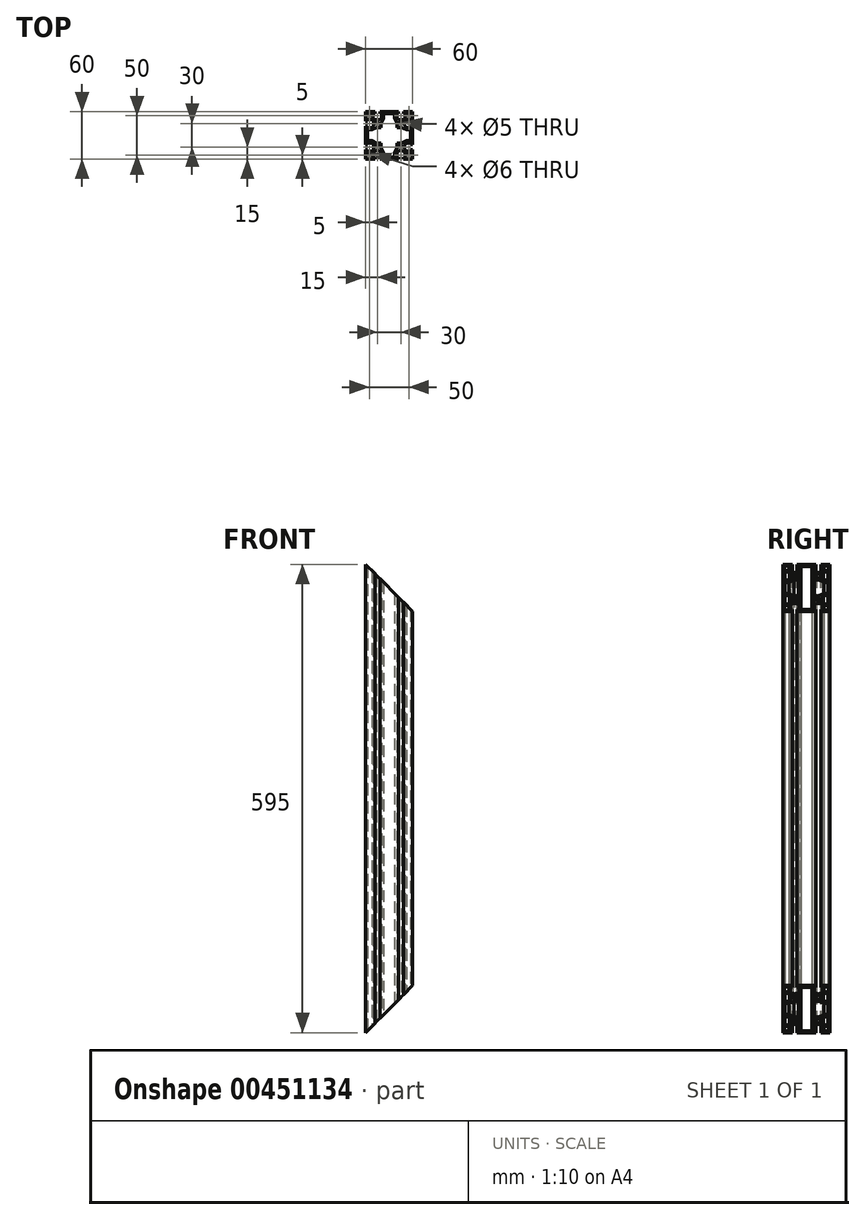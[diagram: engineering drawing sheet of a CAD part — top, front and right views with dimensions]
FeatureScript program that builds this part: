
annotation { "Feature Type Name" : "Feature", "Feature Type Description" : "" }
export const myFeature = defineFeature(function(context is Context, id is Id, definition is map)
    precondition{}
    {
        {
            var Q0;
            Q0=qCreatedBy(makeId("Top.planeOp"),FACE);
            var sketch = newSketch(context, id + "F0", { "sketchPlane" : qUnion([Q0])});
            skLineSegment(sketch, "E0.bottom", {"start": v(30, -30) * mm, "end": v(-30, -30) * mm});
            skLineSegment(sketch, "E0.top", {"start": v(30, 30) * mm, "end": v(-30, 30) * mm});
            skLineSegment(sketch, "E0.left", {"start": v(30, -30) * mm, "end": v(30, 30) * mm});
            skLineSegment(sketch, "E0.right", {"start": v(-30, -30) * mm, "end": v(-30, 30) * mm});
            skPoint(sketch, "E0.middle", {"position": v(0, 0) * mm});
            skLineSegment(sketch, "E1.top", {"start": v(-11.85, 30) * mm, "end": v(-18.15, 30) * mm});
            skLineSegment(sketch, "E1.left", {"start": v(-11.85, 27.5) * mm, "end": v(-11.85, 30) * mm});
            skLineSegment(sketch, "E1.right", {"start": v(-18.15, 27.5) * mm, "end": v(-18.15, 30) * mm});
            skPoint(sketch, "E1.middle", {"position": v(-15, 28.75) * mm});
            skLineSegment(sketch, "E2.bottom", {"start": v(-9.85, 27.5) * mm, "end": v(-11.85, 27.5) * mm});
            skLineSegment(sketch, "E2.left", {"start": v(-9.85, 27.5) * mm, "end": v(-9.85, 21.55) * mm});
            skLineSegment(sketch, "E2.right", {"start": v(-20.15, 27.5) * mm, "end": v(-20.15, 21.55) * mm});
            skPoint(sketch, "E2.middle", {"position": v(-15, 24.52) * mm});
            skArc(sketch, "E3", {"start": v(-20.15, 21.55) * mm, "mid": v(-15, 19.5) * mm, "end": v(-9.85, 21.55) * mm});
            skPoint(sketch, "E4.MirrorP", {"position": v(15, 24.52) * mm});
            skPoint(sketch, "E5.MirrorP", {"position": v(15, 28.75) * mm});
            skLineSegment(sketch, "E6.MirrorCS", {"start": v(11.85, 27.5) * mm, "end": v(11.85, 30) * mm});
            skLineSegment(sketch, "E7.MirrorCS", {"start": v(18.15, 27.5) * mm, "end": v(18.15, 30) * mm});
            skLineSegment(sketch, "E8.MirrorCS", {"start": v(9.85, 27.5) * mm, "end": v(11.85, 27.5) * mm});
            skLineSegment(sketch, "E9.MirrorCS", {"start": v(9.85, 27.5) * mm, "end": v(9.85, 21.55) * mm});
            skArc(sketch, "E10.MirrorCS", {"start": v(20.15, 21.55) * mm, "mid": v(15, 19.5) * mm, "end": v(9.85, 21.55) * mm});
            skLineSegment(sketch, "E11.MirrorCS", {"start": v(20.15, 27.5) * mm, "end": v(20.15, 21.55) * mm});
            skLineSegment(sketch, "E12.MirrorCS", {"start": v(11.85, 30) * mm, "end": v(18.15, 30) * mm});
            skLineSegment(sketch, "E13.1.0", {"start": v(27.5, 20.15) * mm, "end": v(21.55, 20.15) * mm});
            skLineSegment(sketch, "E13.1.1", {"start": v(27.5, 9.85) * mm, "end": v(21.55, 9.85) * mm});
            skArc(sketch, "E13.1.2", {"start": v(21.55, 20.15) * mm, "mid": v(19.5, 15) * mm, "end": v(21.55, 9.85) * mm});
            skLineSegment(sketch, "E13.1.3", {"start": v(27.5, -9.85) * mm, "end": v(21.55, -9.85) * mm});
            skLineSegment(sketch, "E13.1.4", {"start": v(27.5, -20.15) * mm, "end": v(21.55, -20.15) * mm});
            skPoint(sketch, "E13.1.5", {"position": v(28.75, 15) * mm});
            skPoint(sketch, "E13.1.6", {"position": v(28.75, -15) * mm});
            skArc(sketch, "E13.1.7", {"start": v(21.55, -20.15) * mm, "mid": v(19.5, -15) * mm, "end": v(21.55, -9.85) * mm});
            skPoint(sketch, "E13.1.8", {"position": v(24.52, -15) * mm});
            skPoint(sketch, "E13.1.9", {"position": v(24.52, 15) * mm});
            skLineSegment(sketch, "E13.1.10", {"start": v(27.5, 9.85) * mm, "end": v(27.5, 20.15) * mm});
            skLineSegment(sketch, "E13.1.11", {"start": v(27.5, -11.85) * mm, "end": v(27.5, -18.15) * mm});
            skLineSegment(sketch, "E13.1.12", {"start": v(30, 11.85) * mm, "end": v(30, 18.15) * mm});
            skLineSegment(sketch, "E13.1.13", {"start": v(30, -11.85) * mm, "end": v(30, -18.15) * mm});
            skLineSegment(sketch, "E13.1.14", {"start": v(27.5, 18.15) * mm, "end": v(30, 18.15) * mm});
            skLineSegment(sketch, "E13.1.15", {"start": v(27.5, 11.85) * mm, "end": v(30, 11.85) * mm});
            skLineSegment(sketch, "E13.1.16", {"start": v(27.5, 11.85) * mm, "end": v(27.5, 18.15) * mm});
            skLineSegment(sketch, "E13.1.17", {"start": v(27.5, -9.85) * mm, "end": v(27.5, -20.15) * mm});
            skLineSegment(sketch, "E13.1.18", {"start": v(27.5, -18.15) * mm, "end": v(30, -18.15) * mm});
            skLineSegment(sketch, "E13.1.19", {"start": v(27.5, -11.85) * mm, "end": v(30, -11.85) * mm});
            skLineSegment(sketch, "E13.2.0", {"start": v(20.15, -27.5) * mm, "end": v(20.15, -21.55) * mm});
            skLineSegment(sketch, "E13.2.1", {"start": v(9.85, -27.5) * mm, "end": v(9.85, -21.55) * mm});
            skArc(sketch, "E13.2.2", {"start": v(20.15, -21.55) * mm, "mid": v(15, -19.5) * mm, "end": v(9.85, -21.55) * mm});
            skLineSegment(sketch, "E13.2.3", {"start": v(-9.85, -27.5) * mm, "end": v(-9.85, -21.55) * mm});
            skLineSegment(sketch, "E13.2.4", {"start": v(-20.15, -27.5) * mm, "end": v(-20.15, -21.55) * mm});
            skPoint(sketch, "E13.2.5", {"position": v(15, -28.75) * mm});
            skPoint(sketch, "E13.2.6", {"position": v(-15, -28.75) * mm});
            skArc(sketch, "E13.2.7", {"start": v(-20.15, -21.55) * mm, "mid": v(-15, -19.5) * mm, "end": v(-9.85, -21.55) * mm});
            skPoint(sketch, "E13.2.8", {"position": v(-15, -24.52) * mm});
            skPoint(sketch, "E13.2.9", {"position": v(15, -24.52) * mm});
            skLineSegment(sketch, "E13.2.10", {"start": v(9.85, -27.5) * mm, "end": v(20.15, -27.5) * mm});
            skLineSegment(sketch, "E13.2.11", {"start": v(-11.85, -27.5) * mm, "end": v(-18.15, -27.5) * mm});
            skLineSegment(sketch, "E13.2.12", {"start": v(11.85, -30) * mm, "end": v(18.15, -30) * mm});
            skLineSegment(sketch, "E13.2.13", {"start": v(-11.85, -30) * mm, "end": v(-18.15, -30) * mm});
            skLineSegment(sketch, "E13.2.14", {"start": v(18.15, -27.5) * mm, "end": v(18.15, -30) * mm});
            skLineSegment(sketch, "E13.2.15", {"start": v(11.85, -27.5) * mm, "end": v(11.85, -30) * mm});
            skLineSegment(sketch, "E13.2.16", {"start": v(11.85, -27.5) * mm, "end": v(18.15, -27.5) * mm});
            skLineSegment(sketch, "E13.2.17", {"start": v(-9.85, -27.5) * mm, "end": v(-20.15, -27.5) * mm});
            skLineSegment(sketch, "E13.2.18", {"start": v(-18.15, -27.5) * mm, "end": v(-18.15, -30) * mm});
            skLineSegment(sketch, "E13.2.19", {"start": v(-11.85, -27.5) * mm, "end": v(-11.85, -30) * mm});
            skLineSegment(sketch, "E13.3.0", {"start": v(-27.5, -20.15) * mm, "end": v(-21.55, -20.15) * mm});
            skLineSegment(sketch, "E13.3.1", {"start": v(-27.5, -9.85) * mm, "end": v(-21.55, -9.85) * mm});
            skArc(sketch, "E13.3.2", {"start": v(-21.55, -20.15) * mm, "mid": v(-19.5, -15) * mm, "end": v(-21.55, -9.85) * mm});
            skLineSegment(sketch, "E13.3.3", {"start": v(-27.5, 9.85) * mm, "end": v(-21.55, 9.85) * mm});
            skLineSegment(sketch, "E13.3.4", {"start": v(-27.5, 20.15) * mm, "end": v(-21.55, 20.15) * mm});
            skPoint(sketch, "E13.3.5", {"position": v(-28.75, -15) * mm});
            skPoint(sketch, "E13.3.6", {"position": v(-28.75, 15) * mm});
            skArc(sketch, "E13.3.7", {"start": v(-21.55, 20.15) * mm, "mid": v(-19.5, 15) * mm, "end": v(-21.55, 9.85) * mm});
            skPoint(sketch, "E13.3.8", {"position": v(-24.52, 15) * mm});
            skPoint(sketch, "E13.3.9", {"position": v(-24.52, -15) * mm});
            skLineSegment(sketch, "E13.3.10", {"start": v(-27.5, -9.85) * mm, "end": v(-27.5, -20.15) * mm});
            skLineSegment(sketch, "E13.3.11", {"start": v(-27.5, 11.85) * mm, "end": v(-27.5, 18.15) * mm});
            skLineSegment(sketch, "E13.3.12", {"start": v(-30, -11.85) * mm, "end": v(-30, -18.15) * mm});
            skLineSegment(sketch, "E13.3.13", {"start": v(-30, 11.85) * mm, "end": v(-30, 18.15) * mm});
            skLineSegment(sketch, "E13.3.14", {"start": v(-27.5, -18.15) * mm, "end": v(-30, -18.15) * mm});
            skLineSegment(sketch, "E13.3.15", {"start": v(-27.5, -11.85) * mm, "end": v(-30, -11.85) * mm});
            skLineSegment(sketch, "E13.3.16", {"start": v(-27.5, -11.85) * mm, "end": v(-27.5, -18.15) * mm});
            skLineSegment(sketch, "E13.3.17", {"start": v(-27.5, 9.85) * mm, "end": v(-27.5, 20.15) * mm});
            skLineSegment(sketch, "E13.3.18", {"start": v(-27.5, 18.15) * mm, "end": v(-30, 18.15) * mm});
            skLineSegment(sketch, "E13.3.19", {"start": v(-27.5, 11.85) * mm, "end": v(-30, 11.85) * mm});
            skLineSegment(sketch, "E13.anchor1", {"start": v(0, 0) * mm, "end": v(-20.15, 21.55) * mm, "construction": true});
            skLineSegment(sketch, "E13.anchor2", {"start": v(0, 0) * mm, "end": v(-21.55, -20.15) * mm, "construction": true});
            skLineSegment(sketch, "E14.trimOffspring", {"start": v(-18.15, 27.5) * mm, "end": v(-20.15, 27.5) * mm});
            skLineSegment(sketch, "E15.trimOffspring", {"start": v(18.15, 27.5) * mm, "end": v(20.15, 27.5) * mm});
            skCircle(sketch, "E16", {"center": v(-15, 15) * mm, "radius": 2.5 * mm});
            skCircle(sketch, "E17", {"center": v(-25, 25) * mm, "radius": 3 * mm});
            skCircle(sketch, "E18.MirrorC", {"center": v(25, 25) * mm, "radius": 3 * mm});
            skCircle(sketch, "E19.MirrorC", {"center": v(25, -25) * mm, "radius": 3 * mm});
            skCircle(sketch, "E20.MirrorC", {"center": v(-25, -25) * mm, "radius": 3 * mm});
            skCircle(sketch, "E21.MirrorC", {"center": v(15, 15) * mm, "radius": 2.5 * mm});
            skCircle(sketch, "E22.MirrorC", {"center": v(15, -15) * mm, "radius": 2.5 * mm});
            skCircle(sketch, "E23.MirrorC", {"center": v(-15, -15) * mm, "radius": 2.5 * mm});
            skLineSegment(sketch, "E24", {"start": v(-7, 27.5) * mm, "end": v(0, 27.5) * mm});
            skLineSegment(sketch, "E25", {"start": v(-7, 27.5) * mm, "end": v(-7, 22) * mm});
            skLineSegment(sketch, "E26", {"start": v(-10, 10) * mm, "end": v(-10, 16) * mm});
            skLineSegment(sketch, "E27", {"start": v(-10, 16) * mm, "end": v(-7, 22) * mm});
            skLineSegment(sketch, "E28.MirrorCS", {"start": v(10, 10) * mm, "end": v(10, 16) * mm});
            skLineSegment(sketch, "E29.MirrorCS", {"start": v(10, 16) * mm, "end": v(7, 22) * mm});
            skLineSegment(sketch, "E30.MirrorCS", {"start": v(7, 27.5) * mm, "end": v(0, 27.5) * mm});
            skLineSegment(sketch, "E31.MirrorCS", {"start": v(7, 27.5) * mm, "end": v(7, 22) * mm});
            skLineSegment(sketch, "E32.1.0", {"start": v(-10, -10) * mm, "end": v(-16, -10) * mm});
            skLineSegment(sketch, "E32.1.1", {"start": v(-16, -10) * mm, "end": v(-22, -7) * mm});
            skLineSegment(sketch, "E32.1.2", {"start": v(-27.5, -7) * mm, "end": v(-22, -7) * mm});
            skLineSegment(sketch, "E32.1.3", {"start": v(-27.5, -7) * mm, "end": v(-27.5, 0) * mm});
            skLineSegment(sketch, "E32.1.4", {"start": v(-27.5, 7) * mm, "end": v(-27.5, 0) * mm});
            skLineSegment(sketch, "E32.1.5", {"start": v(-27.5, 7) * mm, "end": v(-22, 7) * mm});
            skLineSegment(sketch, "E32.1.6", {"start": v(-16, 10) * mm, "end": v(-22, 7) * mm});
            skLineSegment(sketch, "E32.1.7", {"start": v(-10, 10) * mm, "end": v(-16, 10) * mm});
            skLineSegment(sketch, "E32.2.0", {"start": v(10, -10) * mm, "end": v(10, -16) * mm});
            skLineSegment(sketch, "E32.2.1", {"start": v(10, -16) * mm, "end": v(7, -22) * mm});
            skLineSegment(sketch, "E32.2.2", {"start": v(7, -27.5) * mm, "end": v(7, -22) * mm});
            skLineSegment(sketch, "E32.2.3", {"start": v(7, -27.5) * mm, "end": v(0, -27.5) * mm});
            skLineSegment(sketch, "E32.2.4", {"start": v(-7, -27.5) * mm, "end": v(0, -27.5) * mm});
            skLineSegment(sketch, "E32.2.5", {"start": v(-7, -27.5) * mm, "end": v(-7, -22) * mm});
            skLineSegment(sketch, "E32.2.6", {"start": v(-10, -16) * mm, "end": v(-7, -22) * mm});
            skLineSegment(sketch, "E32.2.7", {"start": v(-10, -10) * mm, "end": v(-10, -16) * mm});
            skLineSegment(sketch, "E32.3.0", {"start": v(10, 10) * mm, "end": v(16, 10) * mm});
            skLineSegment(sketch, "E32.3.1", {"start": v(16, 10) * mm, "end": v(22, 7) * mm});
            skLineSegment(sketch, "E32.3.2", {"start": v(27.5, 7) * mm, "end": v(22, 7) * mm});
            skLineSegment(sketch, "E32.3.3", {"start": v(27.5, 7) * mm, "end": v(27.5, 0) * mm});
            skLineSegment(sketch, "E32.3.4", {"start": v(27.5, -7) * mm, "end": v(27.5, 0) * mm});
            skLineSegment(sketch, "E32.3.5", {"start": v(27.5, -7) * mm, "end": v(22, -7) * mm});
            skLineSegment(sketch, "E32.3.6", {"start": v(16, -10) * mm, "end": v(22, -7) * mm});
            skLineSegment(sketch, "E32.3.7", {"start": v(10, -10) * mm, "end": v(16, -10) * mm});
            skSolve(sketch);
        }
        {
            var Q0;
            {var subQ30=sQuery(id+"F0.wireOp",EDGE,"E1.left");Q0=makeQuery(id+"F0.imprint","IMPRINT",FACE,{"disambiguationData":[TD([[makeQuery(id+"F0.imprint","IMPRINT",EDGE,{"derivedFrom":subQ30}),-1.0]])]});}
            extrude(context, id + "F1", {"entities" : qUnion([Q0]), "depth" : 595 * mm});
        }
        {
            var Q0;
            Q0=makeQuery(id+"F1.opExtrude","SWEPT_EDGE",EDGE,{"disambiguationData":[OSD([sQuery(id+"F0.wireOp",EDGE,"E24"),sQuery(id+"F0.wireOp",EDGE,"E25")])]});
            var Q1;
            Q1=makeQuery(id+"F1.opExtrude","SWEPT_EDGE",EDGE,{"disambiguationData":[OSD([sQuery(id+"F0.wireOp",EDGE,"E30.MirrorCS"),sQuery(id+"F0.wireOp",EDGE,"E31.MirrorCS")])]});
            var Q2;
            Q2=makeQuery(id+"F1.opExtrude","SWEPT_EDGE",EDGE,{"disambiguationData":[OSD([sQuery(id+"F0.wireOp",EDGE,"840db5bc-c403-45cd-90c7-254e62d9e8c5.3.2"),sQuery(id+"F0.wireOp",EDGE,"840db5bc-c403-45cd-90c7-254e62d9e8c5.3.3")])]});
            var Q3;
            Q3=makeQuery(id+"F1.opExtrude","SWEPT_EDGE",EDGE,{"disambiguationData":[OSD([sQuery(id+"F0.wireOp",EDGE,"840db5bc-c403-45cd-90c7-254e62d9e8c5.3.4"),sQuery(id+"F0.wireOp",EDGE,"840db5bc-c403-45cd-90c7-254e62d9e8c5.3.5")])]});
            var Q4;
            Q4=makeQuery(id+"F1.opExtrude","SWEPT_EDGE",EDGE,{"disambiguationData":[OSD([sQuery(id+"F0.wireOp",EDGE,"840db5bc-c403-45cd-90c7-254e62d9e8c5.1.4"),sQuery(id+"F0.wireOp",EDGE,"840db5bc-c403-45cd-90c7-254e62d9e8c5.1.5")])]});
            var Q5;
            Q5=makeQuery(id+"F1.opExtrude","SWEPT_EDGE",EDGE,{"disambiguationData":[OSD([sQuery(id+"F0.wireOp",EDGE,"840db5bc-c403-45cd-90c7-254e62d9e8c5.1.2"),sQuery(id+"F0.wireOp",EDGE,"840db5bc-c403-45cd-90c7-254e62d9e8c5.1.3")])]});
            var Q6;
            Q6=makeQuery(id+"F1.opExtrude","SWEPT_EDGE",EDGE,{"disambiguationData":[OSD([sQuery(id+"F0.wireOp",EDGE,"840db5bc-c403-45cd-90c7-254e62d9e8c5.2.2"),sQuery(id+"F0.wireOp",EDGE,"840db5bc-c403-45cd-90c7-254e62d9e8c5.2.3")])]});
            var Q7;
            Q7=makeQuery(id+"F1.opExtrude","SWEPT_EDGE",EDGE,{"disambiguationData":[OSD([sQuery(id+"F0.wireOp",EDGE,"840db5bc-c403-45cd-90c7-254e62d9e8c5.2.4"),sQuery(id+"F0.wireOp",EDGE,"840db5bc-c403-45cd-90c7-254e62d9e8c5.2.5")])]});
            fillet(context, id + "F2", {"entities" : qUnion([Q0, Q1, Q2, Q3, Q4, Q5, Q6, Q7]), "radius" : 2 * mm, "tangentPropagation" : true, "allowEdgeOverflow" : false});
        }
        {
            var Q0;
            Q0=makeQuery(id+"F1.opExtrude","SWEPT_EDGE",EDGE,{"disambiguationData":[OSD([sQuery(id+"F0.wireOp",EDGE,"E26"),sQuery(id+"F0.wireOp",EDGE,"E27")])]});
            var Q1;
            Q1=makeQuery(id+"F1.opExtrude","SWEPT_EDGE",EDGE,{"disambiguationData":[OSD([sQuery(id+"F0.wireOp",EDGE,"E28.MirrorCS"),sQuery(id+"F0.wireOp",EDGE,"E29.MirrorCS")])]});
            var Q2;
            Q2=makeQuery(id+"F1.opExtrude","SWEPT_EDGE",EDGE,{"disambiguationData":[OSD([sQuery(id+"F0.wireOp",EDGE,"840db5bc-c403-45cd-90c7-254e62d9e8c5.3.0"),sQuery(id+"F0.wireOp",EDGE,"840db5bc-c403-45cd-90c7-254e62d9e8c5.3.1")])]});
            var Q3;
            Q3=makeQuery(id+"F1.opExtrude","SWEPT_EDGE",EDGE,{"disambiguationData":[OSD([sQuery(id+"F0.wireOp",EDGE,"840db5bc-c403-45cd-90c7-254e62d9e8c5.1.6"),sQuery(id+"F0.wireOp",EDGE,"840db5bc-c403-45cd-90c7-254e62d9e8c5.1.7")])]});
            var Q4;
            Q4=makeQuery(id+"F1.opExtrude","SWEPT_EDGE",EDGE,{"disambiguationData":[OSD([sQuery(id+"F0.wireOp",EDGE,"840db5bc-c403-45cd-90c7-254e62d9e8c5.1.0"),sQuery(id+"F0.wireOp",EDGE,"840db5bc-c403-45cd-90c7-254e62d9e8c5.1.1")])]});
            var Q5;
            Q5=makeQuery(id+"F1.opExtrude","SWEPT_EDGE",EDGE,{"disambiguationData":[OSD([sQuery(id+"F0.wireOp",EDGE,"840db5bc-c403-45cd-90c7-254e62d9e8c5.3.6"),sQuery(id+"F0.wireOp",EDGE,"840db5bc-c403-45cd-90c7-254e62d9e8c5.3.7")])]});
            var Q6;
            Q6=makeQuery(id+"F1.opExtrude","SWEPT_EDGE",EDGE,{"disambiguationData":[OSD([sQuery(id+"F0.wireOp",EDGE,"840db5bc-c403-45cd-90c7-254e62d9e8c5.2.0"),sQuery(id+"F0.wireOp",EDGE,"840db5bc-c403-45cd-90c7-254e62d9e8c5.2.1")])]});
            var Q7;
            Q7=makeQuery(id+"F1.opExtrude","SWEPT_EDGE",EDGE,{"disambiguationData":[OSD([sQuery(id+"F0.wireOp",EDGE,"840db5bc-c403-45cd-90c7-254e62d9e8c5.2.6"),sQuery(id+"F0.wireOp",EDGE,"840db5bc-c403-45cd-90c7-254e62d9e8c5.2.7")])]});
            fillet(context, id + "F3", {"entities" : qUnion([Q0, Q1, Q2, Q3, Q4, Q5, Q6, Q7]), "radius" : 7 * mm, "tangentPropagation" : true, "allowEdgeOverflow" : false});
        }
        {
            var Q0;
            {var subQ0=sQuery(id+"F0.wireOp",EDGE,"E0.bottom");Q0=makeQuery(id+"F1.opExtrude","SWEPT_FACE",FACE,{"disambiguationData":[OSD([subQ0]),TDD([makeQuery(id+"F0.imprint","IMPRINT",EDGE,{"disambiguationData":[TD([[makeQuery(id+"F0.imprint","INTERSECT",VERTEX,{"derivedFrom":[subQ0,sQuery(id+"F0.wireOp",EDGE,"E13.2.12"),sQuery(id+"F0.wireOp",EDGE,"E13.2.15")]}),-1.0]])],"derivedFrom":subQ0})])]});}
            var sketch = newSketch(context, id + "F4", { "sketchPlane" : qUnion([Q0])});
            skLineSegment(sketch, "E33.0", {"start": v(30, 595) * mm, "end": v(30, 0) * mm});
            skLineSegment(sketch, "E33.1", {"start": v(-18.15, 595) * mm, "end": v(-30, 595) * mm});
            skLineSegment(sketch, "E33.2", {"start": v(-18.15, 0) * mm, "end": v(-30, 0) * mm});
            skLineSegment(sketch, "E34", {"start": v(-30, 0) * mm, "end": v(30, 0) * mm});
            skLineSegment(sketch, "E35", {"start": v(30, 60) * mm, "end": v(-30, 0) * mm});
            skLineSegment(sketch, "E36", {"start": v(-30, 595) * mm, "end": v(30, 595) * mm});
            skLineSegment(sketch, "E37", {"start": v(30, 535) * mm, "end": v(-30, 595) * mm});
            skSolve(sketch);
        }
        {
            var Q0;
            Q0 = qSketchRegion(id + "F4", true);
            extrude(context, id + "F5", {"entities" : qUnion([Q0]), "operationType" : NewBodyOperationType.REMOVE, "oppositeDirection" : true, "depth" : 60 * mm});
        }
    });
